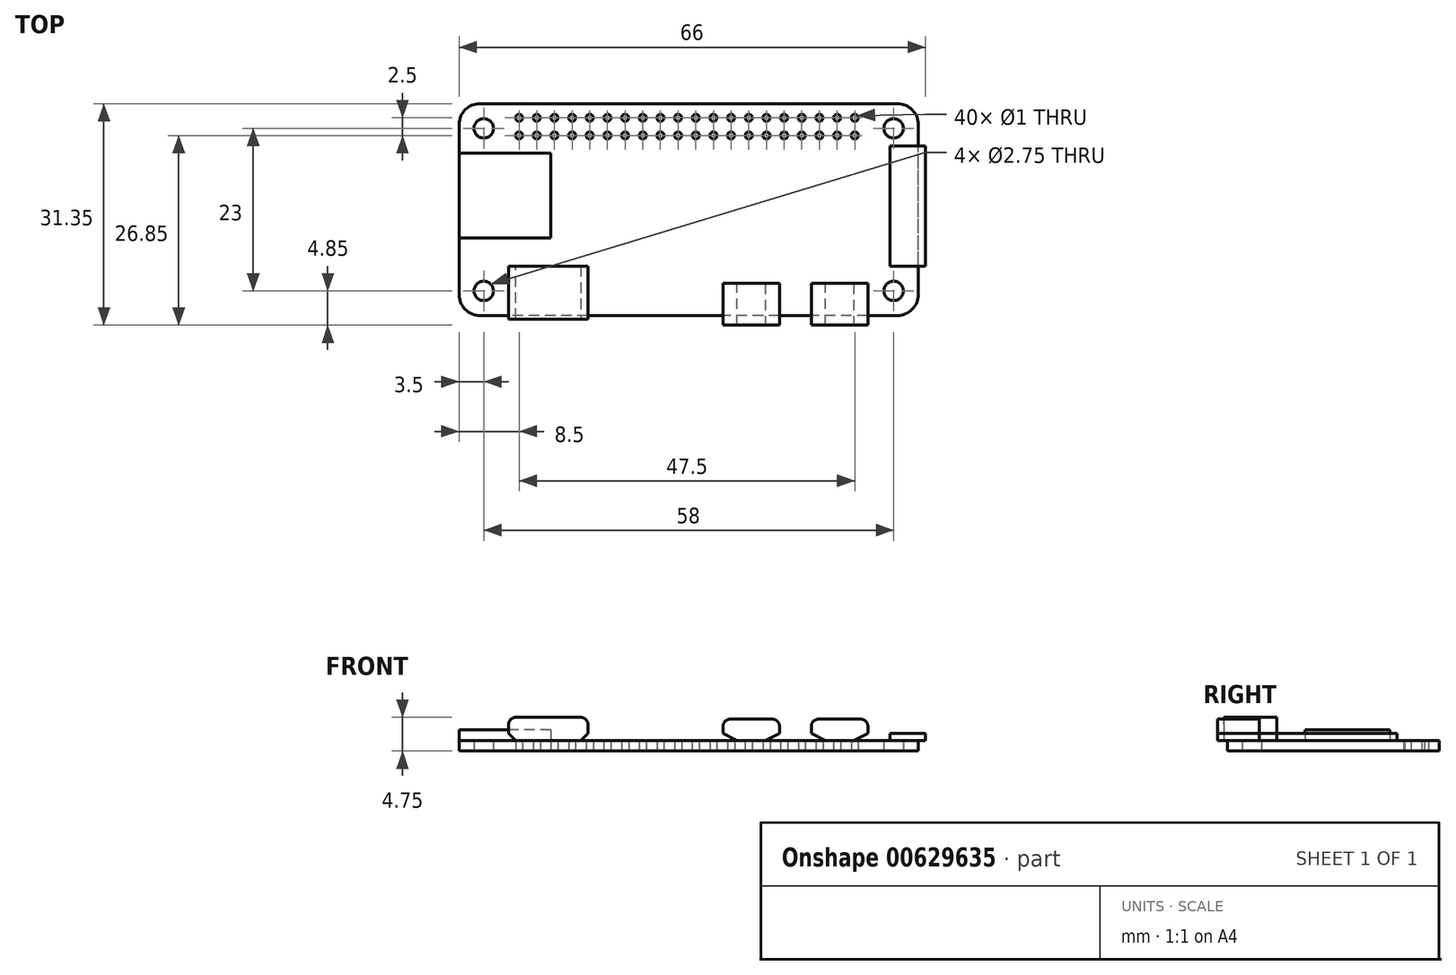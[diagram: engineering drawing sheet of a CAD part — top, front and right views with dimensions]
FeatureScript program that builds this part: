
annotation { "Feature Type Name" : "Feature", "Feature Type Description" : "" }
export const myFeature = defineFeature(function(context is Context, id is Id, definition is map)
    precondition{}
    {
        {
            var Q0;
            Q0=qCreatedBy(makeId("Top.planeOp"),FACE);
            var sketch = newSketch(context, id + "F0", { "sketchPlane" : qUnion([Q0])});
            skLineSegment(sketch, "E0.bottom", {"start": v(29.5, -15) * mm, "end": v(-29.5, -15) * mm});
            skLineSegment(sketch, "E0.top", {"start": v(29.5, 15) * mm, "end": v(-29.5, 15) * mm});
            skLineSegment(sketch, "E0.left", {"start": v(32.5, -12) * mm, "end": v(32.5, 12) * mm});
            skLineSegment(sketch, "E0.right", {"start": v(-32.5, -12) * mm, "end": v(-32.5, 12) * mm});
            skPoint(sketch, "E0.middle", {"position": v(0, 0) * mm});
            skPoint(sketch, "E1.visualSharp", {"position": v(-32.5, 15) * mm});
            skArc(sketch, "E1.filletArc", {"start": v(-29.5, 15) * mm, "mid": v(-31.62, 14.12) * mm, "end": v(-32.5, 12) * mm});
            skPoint(sketch, "E2.visualSharp", {"position": v(-32.5, -15) * mm});
            skArc(sketch, "E2.filletArc", {"start": v(-32.5, -12) * mm, "mid": v(-31.62, -14.12) * mm, "end": v(-29.5, -15) * mm});
            skPoint(sketch, "E3.visualSharp", {"position": v(32.5, -15) * mm});
            skArc(sketch, "E3.filletArc", {"start": v(29.5, -15) * mm, "mid": v(31.62, -14.12) * mm, "end": v(32.5, -12) * mm});
            skPoint(sketch, "E4.visualSharp", {"position": v(32.5, 15) * mm});
            skArc(sketch, "E4.filletArc", {"start": v(32.5, 12) * mm, "mid": v(31.62, 14.12) * mm, "end": v(29.5, 15) * mm});
            skCircle(sketch, "E5", {"center": v(29, 11.5) * mm, "radius": 1.38 * mm});
            skCircle(sketch, "E6.MirrorC", {"center": v(29, -11.5) * mm, "radius": 1.38 * mm});
            skCircle(sketch, "E7.MirrorC", {"center": v(-29, 11.5) * mm, "radius": 1.38 * mm});
            skCircle(sketch, "E8.MirrorC", {"center": v(-29, -11.5) * mm, "radius": 1.38 * mm});
            skCircle(sketch, "E9", {"center": v(-24, 13) * mm, "radius": 0.5 * mm});
            skCircle(sketch, "E10.0.1.0", {"center": v(-24, 10.5) * mm, "radius": 0.5 * mm});
            skCircle(sketch, "E10.1.0.0", {"center": v(-21.5, 13) * mm, "radius": 0.5 * mm});
            skCircle(sketch, "E10.1.1.0", {"center": v(-21.5, 10.5) * mm, "radius": 0.5 * mm});
            skCircle(sketch, "E10.2.0.0", {"center": v(-19, 13) * mm, "radius": 0.5 * mm});
            skCircle(sketch, "E10.2.1.0", {"center": v(-19, 10.5) * mm, "radius": 0.5 * mm});
            skCircle(sketch, "E10.3.0.0", {"center": v(-16.5, 13) * mm, "radius": 0.5 * mm});
            skCircle(sketch, "E10.3.1.0", {"center": v(-16.5, 10.5) * mm, "radius": 0.5 * mm});
            skCircle(sketch, "E10.4.0.0", {"center": v(-14, 13) * mm, "radius": 0.5 * mm});
            skCircle(sketch, "E10.4.1.0", {"center": v(-14, 10.5) * mm, "radius": 0.5 * mm});
            skCircle(sketch, "E10.5.0.0", {"center": v(-11.5, 13) * mm, "radius": 0.5 * mm});
            skCircle(sketch, "E10.5.1.0", {"center": v(-11.5, 10.5) * mm, "radius": 0.5 * mm});
            skCircle(sketch, "E10.6.0.0", {"center": v(-9, 13) * mm, "radius": 0.5 * mm});
            skCircle(sketch, "E10.6.1.0", {"center": v(-9, 10.5) * mm, "radius": 0.5 * mm});
            skCircle(sketch, "E10.7.0.0", {"center": v(-6.5, 13) * mm, "radius": 0.5 * mm});
            skCircle(sketch, "E10.7.1.0", {"center": v(-6.5, 10.5) * mm, "radius": 0.5 * mm});
            skCircle(sketch, "E10.8.0.0", {"center": v(-4, 13) * mm, "radius": 0.5 * mm});
            skCircle(sketch, "E10.8.1.0", {"center": v(-4, 10.5) * mm, "radius": 0.5 * mm});
            skCircle(sketch, "E10.9.0.0", {"center": v(-1.5, 13) * mm, "radius": 0.5 * mm});
            skCircle(sketch, "E10.9.1.0", {"center": v(-1.5, 10.5) * mm, "radius": 0.5 * mm});
            skCircle(sketch, "E10.10.0.0", {"center": v(1, 13) * mm, "radius": 0.5 * mm});
            skCircle(sketch, "E10.10.1.0", {"center": v(1, 10.5) * mm, "radius": 0.5 * mm});
            skCircle(sketch, "E10.11.0.0", {"center": v(3.5, 13) * mm, "radius": 0.5 * mm});
            skCircle(sketch, "E10.11.1.0", {"center": v(3.5, 10.5) * mm, "radius": 0.5 * mm});
            skCircle(sketch, "E10.12.0.0", {"center": v(6, 13) * mm, "radius": 0.5 * mm});
            skCircle(sketch, "E10.12.1.0", {"center": v(6, 10.5) * mm, "radius": 0.5 * mm});
            skCircle(sketch, "E10.13.0.0", {"center": v(8.5, 13) * mm, "radius": 0.5 * mm});
            skCircle(sketch, "E10.13.1.0", {"center": v(8.5, 10.5) * mm, "radius": 0.5 * mm});
            skCircle(sketch, "E10.14.0.0", {"center": v(11, 13) * mm, "radius": 0.5 * mm});
            skCircle(sketch, "E10.14.1.0", {"center": v(11, 10.5) * mm, "radius": 0.5 * mm});
            skCircle(sketch, "E10.15.0.0", {"center": v(13.5, 13) * mm, "radius": 0.5 * mm});
            skCircle(sketch, "E10.15.1.0", {"center": v(13.5, 10.5) * mm, "radius": 0.5 * mm});
            skCircle(sketch, "E10.16.0.0", {"center": v(16, 13) * mm, "radius": 0.5 * mm});
            skCircle(sketch, "E10.16.1.0", {"center": v(16, 10.5) * mm, "radius": 0.5 * mm});
            skCircle(sketch, "E10.17.0.0", {"center": v(18.5, 13) * mm, "radius": 0.5 * mm});
            skCircle(sketch, "E10.17.1.0", {"center": v(18.5, 10.5) * mm, "radius": 0.5 * mm});
            skCircle(sketch, "E10.18.0.0", {"center": v(21, 13) * mm, "radius": 0.5 * mm});
            skCircle(sketch, "E10.18.1.0", {"center": v(21, 10.5) * mm, "radius": 0.5 * mm});
            skCircle(sketch, "E10.19.0.0", {"center": v(23.5, 13) * mm, "radius": 0.5 * mm});
            skCircle(sketch, "E10.19.1.0", {"center": v(23.5, 10.5) * mm, "radius": 0.5 * mm});
            skLineSegment(sketch, "E10.direction1", {"start": v(-24, 13) * mm, "end": v(-21.5, 13) * mm, "construction": true});
            skLineSegment(sketch, "E10.direction2", {"start": v(-24, 13) * mm, "end": v(-24, 10.5) * mm, "construction": true});
            skSolve(sketch);
        }
        {
            var Q0;
            Q0=makeQuery(id+"F0.imprint","IMPRINT",FACE,{"disambiguationData":[TD([[makeQuery(id+"F0.imprint","IMPRINT",EDGE,{"derivedFrom":sQuery(id+"F0.wireOp",EDGE,"E0.bottom")}),-1.0]])]});
            extrude(context, id + "F1", {"entities" : qUnion([Q0]), "depth" : 1.5 * mm, "offsetDistance" : 25 * mm});
        }
        {
            var Q0;
            Q0=makeQuery(id+"F1.opExtrude","CAP_FACE",FACE,{"disambiguationData":[OSD([sQuery(id+"F0.wireOp",EDGE,"E0.bottom"),sQuery(id+"F0.wireOp",EDGE,"E0.top"),sQuery(id+"F0.wireOp",EDGE,"E0.left"),sQuery(id+"F0.wireOp",EDGE,"E0.right"),sQuery(id+"F0.wireOp",EDGE,"E1.filletArc"),sQuery(id+"F0.wireOp",EDGE,"E2.filletArc"),sQuery(id+"F0.wireOp",EDGE,"E3.filletArc"),sQuery(id+"F0.wireOp",EDGE,"E4.filletArc"),sQuery(id+"F0.wireOp",EDGE,"E5"),sQuery(id+"F0.wireOp",EDGE,"E6.MirrorC"),sQuery(id+"F0.wireOp",EDGE,"E7.MirrorC"),sQuery(id+"F0.wireOp",EDGE,"E8.MirrorC")])],"isStart":false});
            var sketch = newSketch(context, id + "F2", { "sketchPlane" : qUnion([Q0])});
            skLineSegment(sketch, "E11.bottom", {"start": v(-19.5, -4) * mm, "end": v(-32.5, -4) * mm});
            skLineSegment(sketch, "E11.top", {"start": v(-19.5, 8) * mm, "end": v(-32.5, 8) * mm});
            skLineSegment(sketch, "E11.left", {"start": v(-19.5, -4) * mm, "end": v(-19.5, 8) * mm});
            skLineSegment(sketch, "E11.right", {"start": v(-32.5, -4) * mm, "end": v(-32.5, 8) * mm});
            skPoint(sketch, "E11.middle", {"position": v(-26, 2) * mm});
            skSolve(sketch);
        }
        {
            var Q0;
            Q0=makeQuery(id+"F2.imprint","IMPRINT",FACE,{"disambiguationData":[TD([[makeQuery(id+"F2.imprint","IMPRINT",EDGE,{"derivedFrom":sQuery(id+"F2.wireOp",EDGE,"E11.bottom")}),-1.0]])]});
            extrude(context, id + "F3", {"entities" : qUnion([Q0]), "depth" : 1.5 * mm, "offsetDistance" : 25 * mm});
        }
        {
            var Q0;
            Q0=makeQuery(id+"F1.opExtrude","CAP_FACE",FACE,{"disambiguationData":[OSD([sQuery(id+"F0.wireOp",EDGE,"E0.bottom"),sQuery(id+"F0.wireOp",EDGE,"E0.top"),sQuery(id+"F0.wireOp",EDGE,"E0.left"),sQuery(id+"F0.wireOp",EDGE,"E0.right"),sQuery(id+"F0.wireOp",EDGE,"E1.filletArc"),sQuery(id+"F0.wireOp",EDGE,"E2.filletArc"),sQuery(id+"F0.wireOp",EDGE,"E3.filletArc"),sQuery(id+"F0.wireOp",EDGE,"E4.filletArc"),sQuery(id+"F0.wireOp",EDGE,"E5"),sQuery(id+"F0.wireOp",EDGE,"E6.MirrorC"),sQuery(id+"F0.wireOp",EDGE,"E7.MirrorC"),sQuery(id+"F0.wireOp",EDGE,"E8.MirrorC")])],"isStart":false});
            var sketch = newSketch(context, id + "F4", { "sketchPlane" : qUnion([Q0])});
            skLineSegment(sketch, "E12.bottom", {"start": v(33.5, -8) * mm, "end": v(28.5, -8) * mm});
            skLineSegment(sketch, "E12.top", {"start": v(33.5, 9) * mm, "end": v(28.5, 9) * mm});
            skLineSegment(sketch, "E12.left", {"start": v(33.5, -8) * mm, "end": v(33.5, 9) * mm});
            skLineSegment(sketch, "E12.right", {"start": v(28.5, -8) * mm, "end": v(28.5, 9) * mm});
            skPoint(sketch, "E12.middle", {"position": v(31, 0.5) * mm});
            skSolve(sketch);
        }
        {
            var Q0;
            {var subQ0=sQuery(id+"F4.wireOp",EDGE,"E12.left");Q0=makeQuery(id+"F4.imprint","IMPRINT",FACE,{"disambiguationData":[TD([[makeQuery(id+"F4.imprint","IMPRINT",EDGE,{"derivedFrom":subQ0}),1.0]])]});}
            var Q1;
            {var subQ0=sQuery(id+"F4.wireOp",EDGE,"E12.right");Q1=makeQuery(id+"F4.imprint","IMPRINT",FACE,{"disambiguationData":[TD([[makeQuery(id+"F4.imprint","IMPRINT",EDGE,{"derivedFrom":subQ0}),-1.0]])]});}
            extrude(context, id + "F5", {"entities" : qUnion([Q0, Q1]), "depth" : 1 * mm, "offsetDistance" : 25 * mm});
        }
        {
            var Q0;
            Q0=makeQuery(id+"F1.opExtrude","CAP_FACE",FACE,{"disambiguationData":[OSD([sQuery(id+"F0.wireOp",EDGE,"E0.bottom"),sQuery(id+"F0.wireOp",EDGE,"E0.top"),sQuery(id+"F0.wireOp",EDGE,"E0.left"),sQuery(id+"F0.wireOp",EDGE,"E0.right"),sQuery(id+"F0.wireOp",EDGE,"E1.filletArc"),sQuery(id+"F0.wireOp",EDGE,"E2.filletArc"),sQuery(id+"F0.wireOp",EDGE,"E3.filletArc"),sQuery(id+"F0.wireOp",EDGE,"E4.filletArc"),sQuery(id+"F0.wireOp",EDGE,"E5"),sQuery(id+"F0.wireOp",EDGE,"E6.MirrorC"),sQuery(id+"F0.wireOp",EDGE,"E7.MirrorC"),sQuery(id+"F0.wireOp",EDGE,"E8.MirrorC")])],"isStart":false});
            var sketch = newSketch(context, id + "F6", { "sketchPlane" : qUnion([Q0])});
            skLineSegment(sketch, "E13.bottom", {"start": v(25.35, -16.35) * mm, "end": v(17.35, -16.35) * mm});
            skLineSegment(sketch, "E13.top", {"start": v(25.35, -10.45) * mm, "end": v(17.35, -10.45) * mm});
            skLineSegment(sketch, "E13.left", {"start": v(25.35, -16.35) * mm, "end": v(25.35, -10.45) * mm});
            skLineSegment(sketch, "E13.right", {"start": v(17.35, -16.35) * mm, "end": v(17.35, -10.45) * mm});
            skPoint(sketch, "E13.middle", {"position": v(21.35, -13.4) * mm});
            skLineSegment(sketch, "E14.bottom", {"start": v(12.85, -16.35) * mm, "end": v(4.85, -16.35) * mm});
            skLineSegment(sketch, "E14.top", {"start": v(12.85, -10.45) * mm, "end": v(4.85, -10.45) * mm});
            skLineSegment(sketch, "E14.left", {"start": v(12.85, -16.35) * mm, "end": v(12.85, -10.45) * mm});
            skLineSegment(sketch, "E14.right", {"start": v(4.85, -16.35) * mm, "end": v(4.85, -10.45) * mm});
            skPoint(sketch, "E14.middle", {"position": v(8.85, -13.4) * mm});
            skSolve(sketch);
        }
        {
            var Q0;
            {var subQ0=sQuery(id+"F6.wireOp",EDGE,"E14.top");Q0=makeQuery(id+"F6.imprint","IMPRINT",FACE,{"disambiguationData":[TD([[makeQuery(id+"F6.imprint","IMPRINT",EDGE,{"derivedFrom":subQ0}),1.0]])]});}
            var Q1;
            {var subQ0=sQuery(id+"F6.wireOp",EDGE,"E14.bottom");Q1=makeQuery(id+"F6.imprint","IMPRINT",FACE,{"disambiguationData":[TD([[makeQuery(id+"F6.imprint","IMPRINT",EDGE,{"derivedFrom":subQ0}),-1.0]])]});}
            var Q2;
            {var subQ0=sQuery(id+"F6.wireOp",EDGE,"E13.top");Q2=makeQuery(id+"F6.imprint","IMPRINT",FACE,{"disambiguationData":[TD([[makeQuery(id+"F6.imprint","IMPRINT",EDGE,{"derivedFrom":subQ0}),1.0]])]});}
            var Q3;
            {var subQ0=sQuery(id+"F6.wireOp",EDGE,"E13.bottom");Q3=makeQuery(id+"F6.imprint","IMPRINT",FACE,{"disambiguationData":[TD([[makeQuery(id+"F6.imprint","IMPRINT",EDGE,{"derivedFrom":subQ0}),-1.0]])]});}
            extrude(context, id + "F7", {"entities" : qUnion([Q0, Q1, Q2, Q3]), "depth" : 3 * mm, "offsetDistance" : 25 * mm});
        }
        {
            var Q0;
            Q0=makeQuery(id+"F7.opExtrude","CAP_EDGE",EDGE,{"disambiguationData":[OSD([sQuery(id+"F6.wireOp",EDGE,"E13.left")])],"isStart":false});
            var Q1;
            Q1=makeQuery(id+"F7.opExtrude","CAP_EDGE",EDGE,{"disambiguationData":[OSD([sQuery(id+"F6.wireOp",EDGE,"E13.right")])],"isStart":false});
            var Q2;
            Q2=makeQuery(id+"F7.opExtrude","CAP_EDGE",EDGE,{"disambiguationData":[OSD([sQuery(id+"F6.wireOp",EDGE,"E14.left")])],"isStart":false});
            var Q3;
            Q3=makeQuery(id+"F7.opExtrude","CAP_EDGE",EDGE,{"disambiguationData":[OSD([sQuery(id+"F6.wireOp",EDGE,"E14.right")])],"isStart":false});
            fillet(context, id + "F8", {"entities" : qUnion([Q0, Q1, Q2, Q3]), "radius" : 1 * mm, "tangentPropagation" : true, "allowEdgeOverflow" : false});
        }
        {
            var Q0;
            Q0=makeQuery(id+"F7.opExtrude","CAP_EDGE",EDGE,{"disambiguationData":[OSD([sQuery(id+"F6.wireOp",EDGE,"E13.left")])],"isStart":true});
            var Q1;
            Q1=makeQuery(id+"F7.opExtrude","CAP_EDGE",EDGE,{"disambiguationData":[OSD([sQuery(id+"F6.wireOp",EDGE,"E13.right")])],"isStart":true});
            var Q2;
            Q2=makeQuery(id+"F7.opExtrude","CAP_EDGE",EDGE,{"disambiguationData":[OSD([sQuery(id+"F6.wireOp",EDGE,"E14.left")])],"isStart":true});
            var Q3;
            Q3=makeQuery(id+"F7.opExtrude","CAP_EDGE",EDGE,{"disambiguationData":[OSD([sQuery(id+"F6.wireOp",EDGE,"E14.right")])],"isStart":true});
            chamfer(context, id + "F9", {"entities" : qUnion([Q0, Q1, Q2, Q3]), "chamferType" : ChamferType.TWO_OFFSETS, "width1" : 1 * mm, "oppositeDirection" : false, "width2" : 2 * mm, "tangentPropagation" : true});
        }
        {
            var Q0;
            Q0=makeQuery(id+"F1.opExtrude","CAP_FACE",FACE,{"disambiguationData":[OSD([sQuery(id+"F0.wireOp",EDGE,"E0.bottom"),sQuery(id+"F0.wireOp",EDGE,"E0.top"),sQuery(id+"F0.wireOp",EDGE,"E0.left"),sQuery(id+"F0.wireOp",EDGE,"E0.right"),sQuery(id+"F0.wireOp",EDGE,"E1.filletArc"),sQuery(id+"F0.wireOp",EDGE,"E2.filletArc"),sQuery(id+"F0.wireOp",EDGE,"E3.filletArc"),sQuery(id+"F0.wireOp",EDGE,"E4.filletArc"),sQuery(id+"F0.wireOp",EDGE,"E5"),sQuery(id+"F0.wireOp",EDGE,"E6.MirrorC"),sQuery(id+"F0.wireOp",EDGE,"E7.MirrorC"),sQuery(id+"F0.wireOp",EDGE,"E8.MirrorC")])],"isStart":false});
            var sketch = newSketch(context, id + "F10", { "sketchPlane" : qUnion([Q0])});
            skLineSegment(sketch, "E15.bottom", {"start": v(-14.25, -15.5) * mm, "end": v(-25.5, -15.5) * mm});
            skLineSegment(sketch, "E15.top", {"start": v(-14.25, -8) * mm, "end": v(-25.5, -8) * mm});
            skLineSegment(sketch, "E15.left", {"start": v(-14.25, -15.5) * mm, "end": v(-14.25, -8) * mm});
            skLineSegment(sketch, "E15.right", {"start": v(-25.5, -15.5) * mm, "end": v(-25.5, -8) * mm});
            skPoint(sketch, "E15.middle", {"position": v(-19.88, -11.75) * mm});
            skSolve(sketch);
        }
        {
            var Q0;
            {var subQ0=sQuery(id+"F10.wireOp",EDGE,"E15.top");Q0=makeQuery(id+"F10.imprint","IMPRINT",FACE,{"disambiguationData":[TD([[makeQuery(id+"F10.imprint","IMPRINT",EDGE,{"derivedFrom":subQ0}),1.0]])]});}
            var Q1;
            {var subQ0=sQuery(id+"F10.wireOp",EDGE,"E15.bottom");Q1=makeQuery(id+"F10.imprint","IMPRINT",FACE,{"disambiguationData":[TD([[makeQuery(id+"F10.imprint","IMPRINT",EDGE,{"derivedFrom":subQ0}),-1.0]])]});}
            extrude(context, id + "F11", {"entities" : qUnion([Q0, Q1]), "depth" : 3.25 * mm, "offsetDistance" : 25 * mm});
        }
        {
            var Q0;
            Q0=makeQuery(id+"F11.opExtrude","CAP_EDGE",EDGE,{"disambiguationData":[OSD([sQuery(id+"F10.wireOp",EDGE,"E15.right")])],"isStart":false});
            var Q1;
            Q1=makeQuery(id+"F11.opExtrude","CAP_EDGE",EDGE,{"disambiguationData":[OSD([sQuery(id+"F10.wireOp",EDGE,"E15.left")])],"isStart":false});
            fillet(context, id + "F12", {"entities" : qUnion([Q0, Q1]), "radius" : 1 * mm, "tangentPropagation" : true, "allowEdgeOverflow" : false});
        }
        {
            var Q0;
            Q0=makeQuery(id+"F11.opExtrude","CAP_EDGE",EDGE,{"disambiguationData":[OSD([sQuery(id+"F10.wireOp",EDGE,"E15.right")])],"isStart":true});
            var Q1;
            Q1=makeQuery(id+"F11.opExtrude","CAP_EDGE",EDGE,{"disambiguationData":[OSD([sQuery(id+"F10.wireOp",EDGE,"E15.left")])],"isStart":true});
            chamfer(context, id + "F13", {"entities" : qUnion([Q0, Q1]), "width" : 1 * mm, "tangentPropagation" : true});
        }
    });
